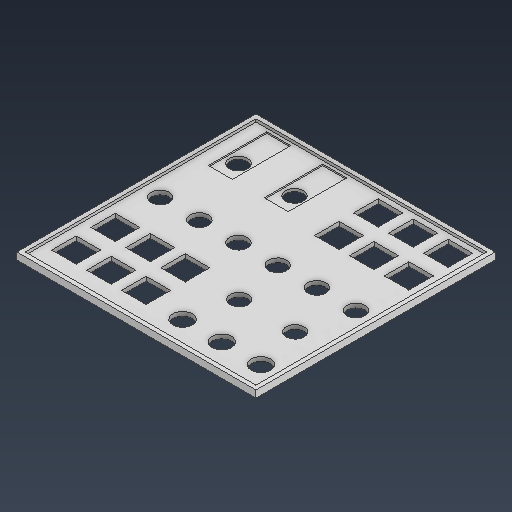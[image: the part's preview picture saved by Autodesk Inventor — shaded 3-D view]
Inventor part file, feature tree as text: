
AUTODESK INVENTOR PART (.ipt)
format: ipt  version: 2025.3 (Build 293356000, 356)  size: 294,400 bytes
history: native  units: mm
features: sketch x6, extrude x4, projected_geometry x2
ambient origin geometry x8: Origin, YZ Plane, XZ Plane, XY Plane, X Axis, Y Axis, Z Axis, Center Point
bodies: Solid1 (feature_tree)
feature tree (12):
  extrude  "Extrusion1"  Depth=171.0mm
  extrude  "Extrusion2"  Depth=2.0mm TaperAngle=0.0deg
  extrude  "Extrusion3"  Depth=1.0mm
  extrude  "Extrusion5"  Depth=60.0mm
  sketch  "Sketch1"  dims[d0=171.0mm d1=171.0mm]
  sketch  "Sketch2"  dims[d7=1.0mm d8=1.0mm]
  projected_geometry  "Projected Loop1"
  sketch  "Sketch3"  dims[d9=60.0mm d10=78.0mm]
  projected_geometry  "Projected Loop2"
  sketch  "Sketch Rectangular Pattern1"  dims[d2=3.0mm d3=0.0mm d5=2.0mm d6=0.0mm]
  sketch  "Sketch Rectangular Pattern4"  dims[d11=78.0mm]
  sketch  "Sketch5"  dims[d12=60.0mm d13=1.0mm d14=1.0mm d15=1.0mm d16=1.0mm d17=75.0mm d19=1.0mm d20=5.0mm d21=30.0mm d22=5.0mm d23=5.0mm d24=1.0mm d27=5.0mm d28=5.0mm d29=1.0mm d30=4.0mm d31=25.0mm d32=17.5mm d33=17.5mm d35=20.0mm d37=28.0mm d38=30.0mm d40=25.0mm d44=5.25mm d45=2.85mm d46=14.0mm d47=11.6mm d49=20.0mm d51=30.0mm d52=17.5mm d53=17.5mm d54=28.0mm d55=25.0mm d57=30.0mm d58=80.0mm d59=25.0mm d60=25.0mm d61=20.0mm d62=40.0mm d63=12.8mm d64=12.8mm d65=10.0mm d66=0.0mm d67=80.0mm d68=16.2mm d69=16.2mm d70=16.2mm d71=28.0mm d72=28.0mm d73=12.0mm d74=14.0mm d75=14.0mm d76=14.0mm d77=13.0mm d78=60.0mm d80=28.0mm d81=10.0mm d83=10.0mm d85=11.5mm d86=163.0mm d87=65.0mm d88=95.0mm d89=88.0mm d90=13.0mm d91=13.0mm d92=30.0mm d93=40.0mm d94=17.5mm d98=165.0mm d99=13.0mm d100=28.8mm d101=17.2mm d102=17.2mm d103=1.0mm d104=0.0mm d105=20.4mm d106=20.4mm]
